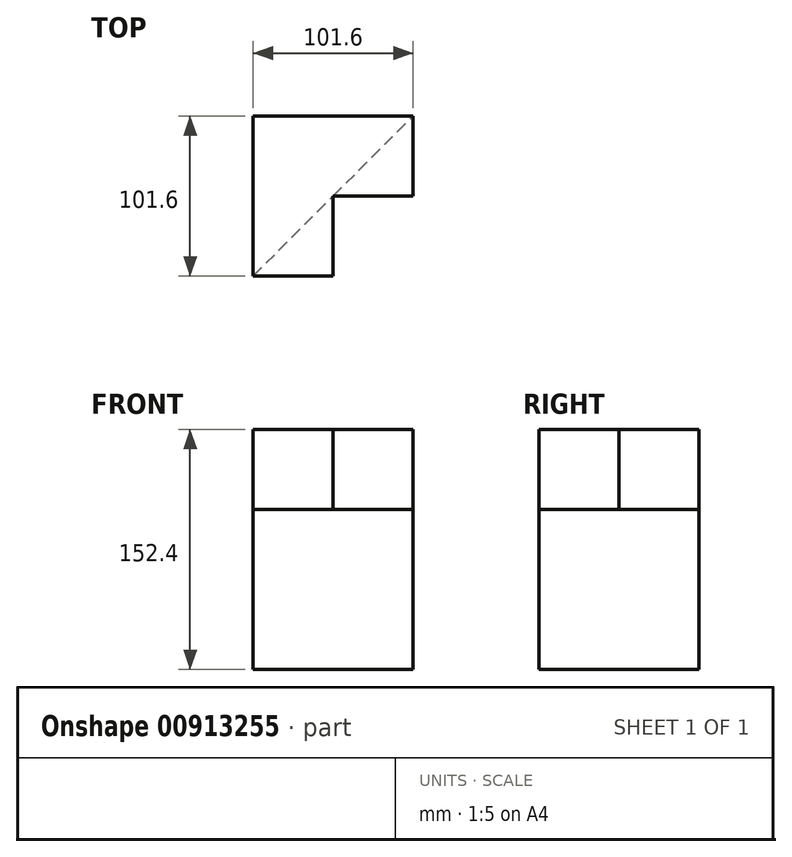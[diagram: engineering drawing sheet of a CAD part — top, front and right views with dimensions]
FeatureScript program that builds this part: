
annotation { "Feature Type Name" : "Feature", "Feature Type Description" : "" }
export const myFeature = defineFeature(function(context is Context, id is Id, definition is map)
    precondition{}
    {
        {
            var Q0;
            Q0=qCreatedBy(makeId("Top.planeOp"),FACE);
            var sketch = newSketch(context, id + "F0", { "sketchPlane" : qUnion([Q0])});
            skLineSegment(sketch, "E0.bottom", {"start": v(0, 0) * mm, "end": v(101.6, 0) * mm});
            skLineSegment(sketch, "E0.top", {"start": v(0, -101.6) * mm, "end": v(101.6, -101.6) * mm});
            skLineSegment(sketch, "E0.left", {"start": v(0, 0) * mm, "end": v(0, -101.6) * mm});
            skLineSegment(sketch, "E0.right", {"start": v(101.6, 0) * mm, "end": v(101.6, -101.6) * mm});
            skLineSegment(sketch, "E1", {"start": v(0, -101.6) * mm, "end": v(101.6, 0) * mm});
            skSolve(sketch);
        }
        {
            var Q0;
            Q0=makeQuery(id+"F0.imprint","IMPRINT",FACE,{"disambiguationData":[TD([[makeQuery(id+"F0.imprint","IMPRINT",EDGE,{"derivedFrom":sQuery(id+"F0.wireOp",EDGE,"E0.bottom")}),-1.0]])]});
            extrude(context, id + "F1", {"entities" : qUnion([Q0]), "depth" : 101.6 * mm, "offsetDistance" : 25.4 * mm});
        }
        {
            var Q0;
            Q0=makeQuery(id+"F1.opExtrude","CAP_FACE",FACE,{"disambiguationData":[OSD([sQuery(id+"F0.wireOp",EDGE,"E0.bottom"),sQuery(id+"F0.wireOp",EDGE,"E0.left"),sQuery(id+"F0.wireOp",EDGE,"E1")])],"isStart":false});
            var sketch = newSketch(context, id + "F2", { "sketchPlane" : qUnion([Q0])});
            skLineSegment(sketch, "E2.bottom", {"start": v(0, 0) * mm, "end": v(101.6, 0) * mm});
            skLineSegment(sketch, "E2.top", {"start": v(0, -101.6) * mm, "end": v(101.6, -101.6) * mm});
            skLineSegment(sketch, "E2.left", {"start": v(0, 0) * mm, "end": v(0, -101.6) * mm});
            skLineSegment(sketch, "E2.right", {"start": v(101.6, 0) * mm, "end": v(101.6, -101.6) * mm});
            skSolve(sketch);
        }
        {
            var Q0;
            Q0=makeQuery(id+"F2.imprint","IMPRINT",FACE,{"disambiguationData":[TD([[makeQuery(id+"F2.imprint","IMPRINT",EDGE,{"derivedFrom":sQuery(id+"F2.wireOp",EDGE,"E2.bottom")}),-1.0]])]});
            var Q1;
            Q1=makeQuery(id+"F2.imprint","IMPRINT",FACE,{"disambiguationData":[TD([[makeQuery(id+"F2.imprint","IMPRINT",EDGE,{"derivedFrom":sQuery(id+"F2.wireOp",EDGE,"E2.top")}),1.0]])]});
            extrude(context, id + "F3", {"entities" : qUnion([Q0, Q1]), "operationType" : NewBodyOperationType.ADD, "depth" : 50.8 * mm, "offsetDistance" : 25.4 * mm});
        }
        {
            var Q0;
            Q0=makeQuery(id+"F3.opExtrude","CAP_FACE",FACE,{"disambiguationData":[OSD([sQuery(id+"F2.wireOp",EDGE,"E2.bottom"),sQuery(id+"F2.wireOp",EDGE,"E2.top"),sQuery(id+"F2.wireOp",EDGE,"E2.left"),sQuery(id+"F2.wireOp",EDGE,"E2.right")])],"isStart":false});
            var sketch = newSketch(context, id + "F4", { "sketchPlane" : qUnion([Q0])});
            skPoint(sketch, "E3.oppositeSnap0", {"position": v(50.8, -101.6) * mm});
            skLineSegment(sketch, "E3.bottom", {"start": v(101.6, -101.6) * mm, "end": v(50.8, -101.6) * mm});
            skLineSegment(sketch, "E3.top", {"start": v(101.6, -50.8) * mm, "end": v(50.8, -50.8) * mm});
            skLineSegment(sketch, "E3.left", {"start": v(101.6, -101.6) * mm, "end": v(101.6, -50.8) * mm});
            skLineSegment(sketch, "E3.right", {"start": v(50.8, -101.6) * mm, "end": v(50.8, -50.8) * mm});
            skSolve(sketch);
        }
        {
            var Q0;
            Q0=makeQuery(id+"F4.imprint","IMPRINT",FACE,{"disambiguationData":[TD([[makeQuery(id+"F4.imprint","IMPRINT",EDGE,{"derivedFrom":sQuery(id+"F4.wireOp",EDGE,"E3.bottom")}),1.0]])]});
            extrude(context, id + "F5", {"entities" : qUnion([Q0]), "operationType" : NewBodyOperationType.REMOVE, "endBound" : BoundingType.THROUGH_ALL, "oppositeDirection" : true, "depth" : 0 * mm, "offsetDistance" : 25.4 * mm});
        }
    });
